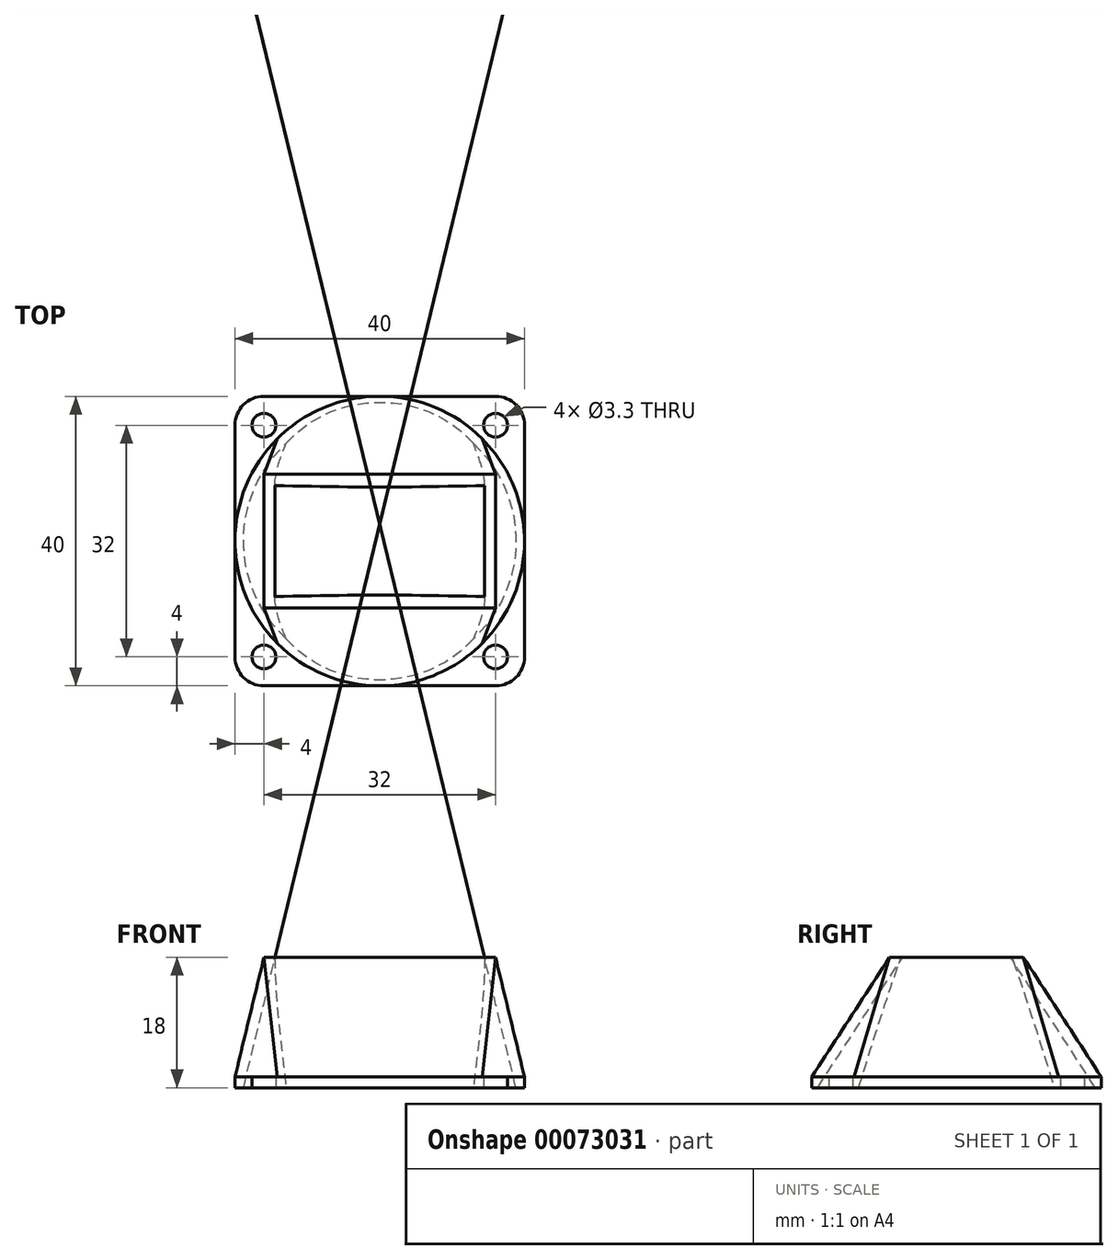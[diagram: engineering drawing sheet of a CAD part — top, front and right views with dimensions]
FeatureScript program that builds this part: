
annotation { "Feature Type Name" : "Feature", "Feature Type Description" : "" }
export const myFeature = defineFeature(function(context is Context, id is Id, definition is map)
    precondition{}
    {
        {
            var Q0;
            Q0=qCreatedBy(makeId("Top.planeOp"),FACE);
            var sketch = newSketch(context, id + "F0", { "sketchPlane" : qUnion([Q0])});
            skLineSegment(sketch, "E0.bottom", {"start": v(-16, 20) * mm, "end": v(16, 20) * mm});
            skLineSegment(sketch, "E0.top", {"start": v(-16, -20) * mm, "end": v(16, -20) * mm});
            skLineSegment(sketch, "E0.left", {"start": v(-20, 16) * mm, "end": v(-20, -16) * mm});
            skLineSegment(sketch, "E0.right", {"start": v(20, 16) * mm, "end": v(20, -16) * mm});
            skLineSegment(sketch, "E1", {"start": v(-20, -20) * mm, "end": v(20, 20) * mm, "construction": true});
            skPoint(sketch, "E2.visualSharp", {"position": v(-20, 20) * mm});
            skArc(sketch, "E2.filletArc", {"start": v(-16, 20) * mm, "mid": v(-18.83, 18.83) * mm, "end": v(-20, 16) * mm});
            skPoint(sketch, "E3.visualSharp", {"position": v(20, 20) * mm});
            skArc(sketch, "E3.filletArc", {"start": v(20, 16) * mm, "mid": v(18.83, 18.83) * mm, "end": v(16, 20) * mm});
            skPoint(sketch, "E4.visualSharp", {"position": v(20, -20) * mm});
            skArc(sketch, "E4.filletArc", {"start": v(16, -20) * mm, "mid": v(18.83, -18.83) * mm, "end": v(20, -16) * mm});
            skPoint(sketch, "E5.visualSharp", {"position": v(-20, -20) * mm});
            skArc(sketch, "E5.filletArc", {"start": v(-20, -16) * mm, "mid": v(-18.83, -18.83) * mm, "end": v(-16, -20) * mm});
            skCircle(sketch, "E6", {"center": v(16, 16) * mm, "radius": 1.65 * mm});
            skCircle(sketch, "E7", {"center": v(16, -16) * mm, "radius": 1.65 * mm});
            skCircle(sketch, "E8", {"center": v(-16, -16) * mm, "radius": 1.65 * mm});
            skCircle(sketch, "E9", {"center": v(-16, 16) * mm, "radius": 1.65 * mm});
            skSolve(sketch);
        }
        {
            var Q0;
            Q0 = qSketchRegion(id + "F0", true);
            extrude(context, id + "F1", {"entities" : qUnion([Q0]), "depth" : 1.5 * mm});
        }
        {
            var Q0;
            Q0=makeQuery(id+"F1.opExtrude","CAP_FACE",FACE,{"disambiguationData":[OSD([sQuery(id+"F0.wireOp",EDGE,"E0.bottom"),sQuery(id+"F0.wireOp",EDGE,"E0.top"),sQuery(id+"F0.wireOp",EDGE,"E0.left"),sQuery(id+"F0.wireOp",EDGE,"E0.right"),sQuery(id+"F0.wireOp",EDGE,"E2.filletArc"),sQuery(id+"F0.wireOp",EDGE,"E3.filletArc"),sQuery(id+"F0.wireOp",EDGE,"E4.filletArc"),sQuery(id+"F0.wireOp",EDGE,"E5.filletArc"),sQuery(id+"F0.wireOp",EDGE,"E6"),sQuery(id+"F0.wireOp",EDGE,"E7"),sQuery(id+"F0.wireOp",EDGE,"E8"),sQuery(id+"F0.wireOp",EDGE,"E9")])],"isStart":false});
            var sketch = newSketch(context, id + "F2", { "sketchPlane" : qUnion([Q0])});
            skCircle(sketch, "E10", {"center": v(0, 0) * mm, "radius": 20 * mm});
            skLineSegment(sketch, "E11.bottom", {"start": v(-14.14, 14.14) * mm, "end": v(14.14, 14.14) * mm, "construction": true});
            skLineSegment(sketch, "E11.top", {"start": v(-14.14, -14.14) * mm, "end": v(14.14, -14.14) * mm, "construction": true});
            skLineSegment(sketch, "E11.left", {"start": v(-14.14, 14.14) * mm, "end": v(-14.14, -14.14) * mm, "construction": true});
            skLineSegment(sketch, "E11.right", {"start": v(14.14, 14.14) * mm, "end": v(14.14, -14.14) * mm, "construction": true});
            skSolve(sketch);
        }
        {
            var Q0;
            {var subQ0=makeQuery(id+"F1.opExtrude","CAP_EDGE",EDGE,{"disambiguationData":[OSD([sQuery(id+"F0.wireOp",EDGE,"E2.filletArc")])],"isStart":false});Q0=makeQuery(id+"F2.imprint","IMPRINT",FACE,{"disambiguationData":[TD([[makeQuery(id+"F2.imprint","IMPRINT",EDGE,{"derivedFrom":subQ0}),1.0]])]});}
            cPlane(context, id + "F3", {"entities" : qUnion([Q0]), "cplaneType" : CPlaneType.OFFSET, "offset" : 16.5 * mm, "width" : 150 * mm, "height" : 150 * mm});
        }
        {
            var Q0;
            Q0=qCreatedBy(id+"F3.planeOp",FACE);
            var sketch = newSketch(context, id + "F4", { "sketchPlane" : qUnion([Q0])});
            skLineSegment(sketch, "E12.bottom", {"start": v(-16, 9.25) * mm, "end": v(16, 9.25) * mm});
            skLineSegment(sketch, "E12.top", {"start": v(-16, -9.25) * mm, "end": v(16, -9.25) * mm});
            skLineSegment(sketch, "E12.left", {"start": v(-16, 9.25) * mm, "end": v(-16, -9.25) * mm});
            skLineSegment(sketch, "E12.right", {"start": v(16, 9.25) * mm, "end": v(16, -9.25) * mm});
            skLineSegment(sketch, "E13", {"start": v(-16, -9.25) * mm, "end": v(16, 9.25) * mm, "construction": true});
            skSolve(sketch);
        }
        {
            var Q0;
            Q0 = qSketchRegion(id + "F2", true);
            var Q1;
            Q1 = qSketchRegion(id + "F4", true);
            var Q2;
            Q2=sQuery(id+"F2.wireOp",VERTEX,"E11.left.end");
            var Q3;
            Q3=sQuery(id+"F4.wireOp",VERTEX,"E13.start");
            loft(context, id + "F5", {"operationType" : NewBodyOperationType.ADD, "sheetProfilesArray" : [{ "sheetProfileEntities" : qUnion([Q0]) }, { "sheetProfileEntities" : qUnion([Q1]) }], "matchConnections" : true, "connections" : [{ "connectionEntities" : qUnion([Q2, Q3]), "connectionEdgeQueries" : qUnion([]), "connectionEdgeParameters" : [] }]});
        }
        {
            var Q0;
            Q0=makeQuery(id+"F5.opLoft","CAP_FACE",FACE,{"disambiguationData":[OSD([makeQuery(id+"F4.imprint","IMPRINT",FACE,{"disambiguationData":[TD([[makeQuery(id+"F4.imprint","IMPRINT",EDGE,{"derivedFrom":sQuery(id+"F4.wireOp",EDGE,"E12.bottom")}),-1.0]])]})])],"isStart":true});
            var Q1;
            Q1=makeQuery(id+"F1.opExtrude","CAP_FACE",FACE,{"disambiguationData":[OSD([sQuery(id+"F0.wireOp",EDGE,"E0.bottom"),sQuery(id+"F0.wireOp",EDGE,"E0.top"),sQuery(id+"F0.wireOp",EDGE,"E0.left"),sQuery(id+"F0.wireOp",EDGE,"E0.right"),sQuery(id+"F0.wireOp",EDGE,"E2.filletArc"),sQuery(id+"F0.wireOp",EDGE,"E3.filletArc"),sQuery(id+"F0.wireOp",EDGE,"E4.filletArc"),sQuery(id+"F0.wireOp",EDGE,"E5.filletArc"),sQuery(id+"F0.wireOp",EDGE,"E6"),sQuery(id+"F0.wireOp",EDGE,"E7"),sQuery(id+"F0.wireOp",EDGE,"E8"),sQuery(id+"F0.wireOp",EDGE,"E9")])],"isStart":true});
            shell(context, id + "F6", {"entities" : qUnion([Q0, Q1]), "thickness" : 1.5 * mm});
        }
    });
